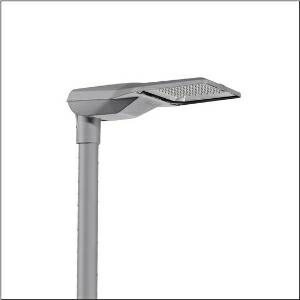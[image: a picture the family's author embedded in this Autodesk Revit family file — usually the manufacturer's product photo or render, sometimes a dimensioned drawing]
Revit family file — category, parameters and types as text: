
# Revit family: streetlight_sl_21_iq_midi___st0_8a_5xe3c31g08mb_0ba1
name_source: partatom
category: Lighting Fixtures
units: mm (PartAtom-declared; Revit-internal decimal feet)

## family parameters
Cut with Voids When Loaded = No
Host = Face
Light Source = No
Part Type = Normal
Room Calculation Point = No
Round Connector Dimension = Use Diameter
Shared = No

## types (1)
- --- (1 x LED, 19500 lm, 146.7 W, 3000K)
    Apparent Load = 147 VA
    CIE Flux Codes = 38 75 97 100 100
    Color Rendering = 70
    Color Temperature = 3000K
    Default Elevation = 1800 mm
    Description = Streetlight SL 21 iQ midi, mast luminaire, primary light control with lens, of PMMA, primary optical cover: cover, of toughened safety glass, transparent, light distribution: ST0.8a, light emission: direct distribution, primary light characteristic: asymmetric, installation type: post-top, side-entry, LED, High Power LED, rated luminous flux: 19.500lm, luminous efficacy: 133lm/W, light colour: 730, colour temperature: 3000K, control gear: iQ Street-Remote, control: Street-Remote, Auto-Match, Temp-Guard, Lumen-Switch, Night-Set, Smart-Wire, Light-Fading, Desk-Remote (wireless, voltage-free reading and setting of iQ features in the workshop via application-optimized NFC function/RFID function), optimised constant luminous flux control (CLO 2.0), pre-setting: linear dimming characteristic, mains connection: 230..240V, AC, 50/60Hz, start of lifetime: 147W, end of service life: 161W, reduction: 62W, luminaire housing, of diecast aluminium, powder-coated, Siteco® metallic grey (DB 702S), corrosivity category C5 mid according to DIN EN ISO 12944, please order mast flange separately, inclination adjustable: 0°, 5°, 10°, 15°, sealing non-destructively replaceable, multi-level sealing system, length: 644mm, width: 335mm, height: 110mm, mast flange for spigot size: 42mm (side-entry): 5XC10008XM4, 60/48mm (side-entry/post-top): 5XC10108XM2, 76/60mm (side-entry/post-top): 5XC10108XM1, mounting height: 4..8m, protection rating (complete): IP66, insulation class (complete): insulation class II (safety insulation), certification: CE, ENEC, ENEC+, VDE, impact resistance: IK10, permissible operating ambient temperature for outdoor applications: -40..+50°C, standard-compliant lighting for roads and squares, packaging unit: 1 piece

Light Distribution: ST0.8a
    Height = 111 mm
    Lamp = 1 x LED
    Lamp Light Flux = 19500 lm
    Lamp Power = 146.7 W
    Lamp count = 1
    Length = 644 mm
    Luminous efficacy = 133 lm/W
    Manufacturer = Siteco
    ModVariant = No
    Model = 5XE3C31G08MB
    Number of Poles = 1
    OnlyDefault = Yes
    Power Factor = 1
    Product Name = Streetlight SL 21 iQ midi | ST0.8a
    Product group = mast luminaire | pylon top
    ProductGroupID = 6100
    Protection Class = Protection class II
    Protection Degree = IP 66
    RLX_Detail_Level = 1
    RLX_Emergency_Light_Flux = 0 lm
    RLX_Emergency_Type = 0
    RLX_Emergency_Type_DB = No
    RlxData = <blob elided: 26941 chars, md5=9864120d>
    Socket = socket
    Standby Power = 0 W
    System Light Flux = 19499 lm
    System Power = 147 W
    Type Comments = factory setting: luminous flux: 100 % | dim-lin: 254 | 753 mA
    Type Image = l_1004298.jpg
    URL = http://relux.com
    VarID = @adj_207519
    Voltage = 0 V
    Weight = 0.00 kg
    Width = 336 mm

## geometry (parser evidence)
native form markers: Blend x4, Sweep x12
no freeform markers — native parametric forms only
